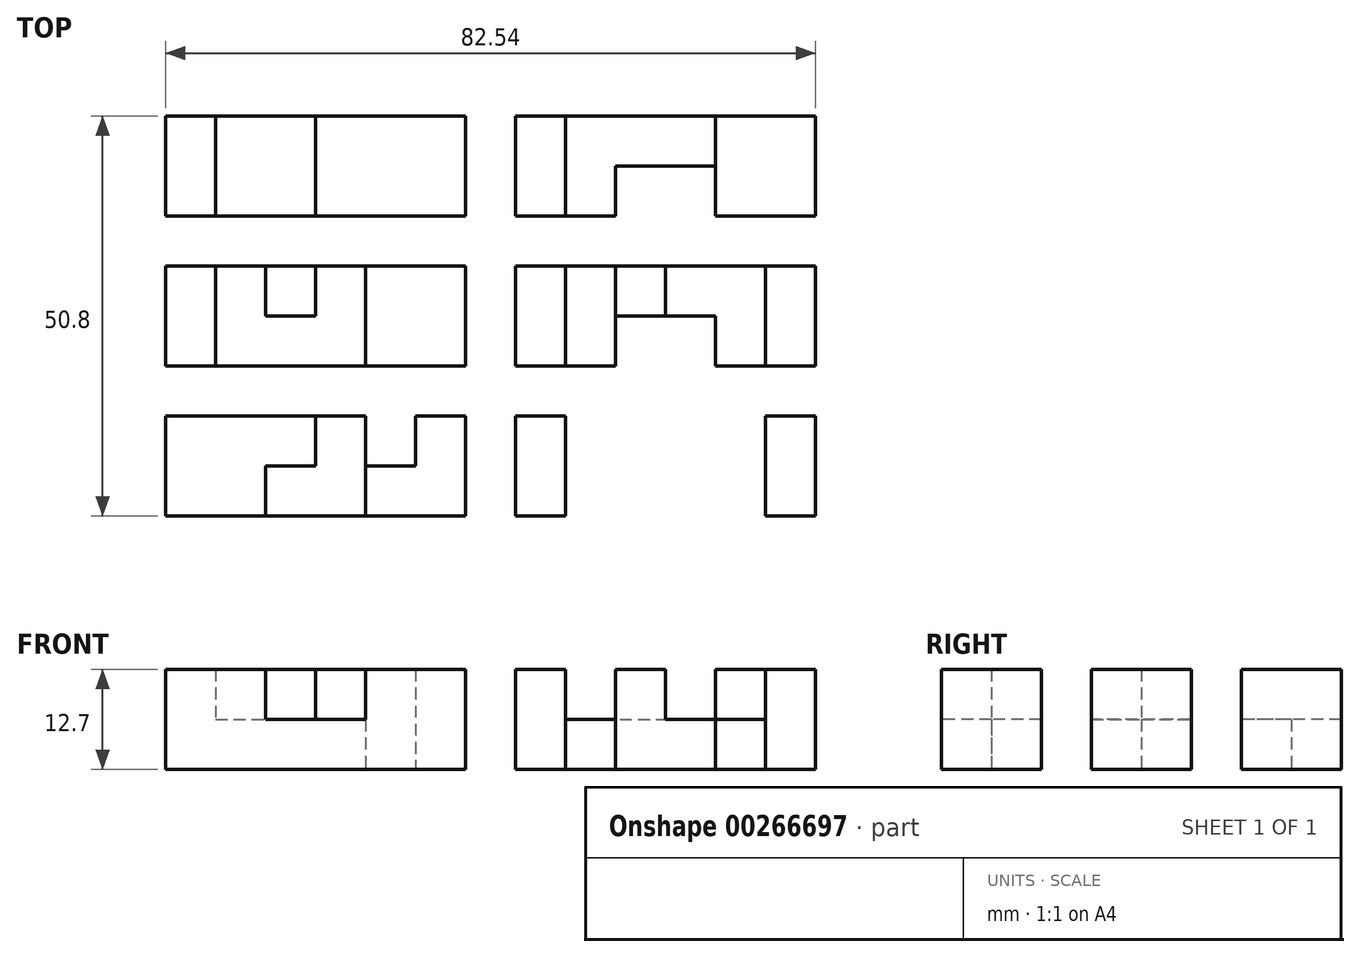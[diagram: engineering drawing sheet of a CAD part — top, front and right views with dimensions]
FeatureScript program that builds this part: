
annotation { "Feature Type Name" : "Feature", "Feature Type Description" : "" }
export const myFeature = defineFeature(function(context is Context, id is Id, definition is map)
    precondition{}
    {
        {
            var Q0;
            Q0=qCreatedBy(makeId("Top.planeOp"),FACE);
            var sketch = newSketch(context, id + "F0", { "sketchPlane" : qUnion([Q0])});
            skLineSegment(sketch, "E0.bottom", {"start": v(41.28, -25.4) * mm, "end": v(28.58, -25.4) * mm});
            skLineSegment(sketch, "E0.left", {"start": v(41.28, -25.4) * mm, "end": v(41.28, -12.7) * mm});
            skLineSegment(sketch, "E0.right", {"start": v(-41.28, -25.4) * mm, "end": v(-41.28, -12.7) * mm});
            skPoint(sketch, "E0.middle", {"position": v(0, 0) * mm});
            skLineSegment(sketch, "E1.right", {"start": v(-3.18, 25.4) * mm, "end": v(-3.18, 12.7) * mm});
            skLineSegment(sketch, "E2.top", {"start": v(41.28, 12.7) * mm, "end": v(28.58, 12.7) * mm});
            skLineSegment(sketch, "E2.left", {"start": v(41.28, 25.4) * mm, "end": v(41.28, 12.7) * mm});
            skLineSegment(sketch, "E2.right", {"start": v(3.18, 25.4) * mm, "end": v(3.18, 12.7) * mm});
            skLineSegment(sketch, "E3.bottom", {"start": v(-41.28, -25.4) * mm, "end": v(-15.88, -25.4) * mm});
            skLineSegment(sketch, "E3.top", {"start": v(-41.28, -12.7) * mm, "end": v(-15.88, -12.7) * mm});
            skLineSegment(sketch, "E3.right", {"start": v(-3.18, -25.4) * mm, "end": v(-3.18, -12.7) * mm});
            skLineSegment(sketch, "E4.top", {"start": v(41.28, -12.7) * mm, "end": v(3.18, -12.7) * mm});
            skLineSegment(sketch, "E4.right", {"start": v(3.17, -25.4) * mm, "end": v(3.17, -12.7) * mm});
            skLineSegment(sketch, "E5", {"start": v(-22.23, 25.4) * mm, "end": v(-22.23, 12.7) * mm});
            skLineSegment(sketch, "E6", {"start": v(28.57, 19.05) * mm, "end": v(15.88, 19.05) * mm});
            skLineSegment(sketch, "E7.right", {"start": v(-34.93, 12.7) * mm, "end": v(-34.93, 25.4) * mm});
            skLineSegment(sketch, "E8.right", {"start": v(-28.57, -19.05) * mm, "end": v(-28.57, -25.4) * mm});
            skLineSegment(sketch, "E9.left", {"start": v(-9.53, -12.7) * mm, "end": v(-9.53, -19.05) * mm});
            skLineSegment(sketch, "E9.right", {"start": v(-15.88, -12.7) * mm, "end": v(-15.88, -25.4) * mm});
            skLineSegment(sketch, "E10", {"start": v(-22.23, -12.7) * mm, "end": v(-22.23, -19.05) * mm});
            skLineSegment(sketch, "E11.top", {"start": v(9.52, -25.4) * mm, "end": v(15.88, -25.4) * mm});
            skLineSegment(sketch, "E11.left", {"start": v(9.52, 25.4) * mm, "end": v(9.52, 12.7) * mm});
            skLineSegment(sketch, "E11.right", {"start": v(15.88, 19.05) * mm, "end": v(15.88, 12.7) * mm});
            skLineSegment(sketch, "E12.top", {"start": v(34.93, -25.4) * mm, "end": v(28.58, -25.4) * mm});
            skLineSegment(sketch, "E12.right", {"start": v(28.57, 25.4) * mm, "end": v(28.58, 12.7) * mm});
            skLineSegment(sketch, "E13.trimOffspring", {"start": v(9.52, -19.05) * mm, "end": v(9.52, -25.4) * mm});
            skLineSegment(sketch, "E14.trimOffspring", {"start": v(15.88, -19.05) * mm, "end": v(15.88, -25.4) * mm});
            skLineSegment(sketch, "E15.trimOffspring", {"start": v(28.58, -19.05) * mm, "end": v(28.58, -25.4) * mm});
            skLineSegment(sketch, "E16.trimOffspring", {"start": v(34.93, -12.7) * mm, "end": v(34.93, -25.4) * mm});
            skLineSegment(sketch, "E17.bottom", {"start": v(-41.28, -6.35) * mm, "end": v(-3.18, -6.35) * mm});
            skLineSegment(sketch, "E17.top", {"start": v(-41.28, 6.35) * mm, "end": v(-3.18, 6.35) * mm});
            skLineSegment(sketch, "E17.left", {"start": v(-41.28, -6.35) * mm, "end": v(-41.28, 6.35) * mm});
            skLineSegment(sketch, "E18.left", {"start": v(-3.18, 6.35) * mm, "end": v(-3.18, -6.35) * mm});
            skLineSegment(sketch, "E18.right", {"start": v(3.18, 6.35) * mm, "end": v(3.18, -6.35) * mm});
            skPoint(sketch, "E19.orphan", {"position": v(41.28, 0) * mm});
            skPoint(sketch, "E20.start.orphan", {"position": v(-41.28, 0) * mm});
            skLineSegment(sketch, "E21.trimOffspring", {"start": v(41.28, 12.7) * mm, "end": v(41.28, 25.4) * mm});
            skLineSegment(sketch, "E22", {"start": v(41.28, 6.35) * mm, "end": v(41.28, -6.35) * mm});
            skLineSegment(sketch, "E23", {"start": v(-28.57, 0) * mm, "end": v(-22.23, 0) * mm});
            skLineSegment(sketch, "E24.trimOffspring", {"start": v(3.18, 6.35) * mm, "end": v(22.23, 6.35) * mm});
            skLineSegment(sketch, "E25.trimOffspring", {"start": v(3.18, -6.35) * mm, "end": v(15.88, -6.35) * mm});
            skLineSegment(sketch, "E26", {"start": v(-34.93, 6.35) * mm, "end": v(-34.93, -6.35) * mm});
            skLineSegment(sketch, "E27", {"start": v(-28.57, 0) * mm, "end": v(-28.57, 6.35) * mm});
            skLineSegment(sketch, "E28", {"start": v(-22.23, 6.35) * mm, "end": v(-22.23, 0) * mm});
            skLineSegment(sketch, "E29", {"start": v(-15.88, -6.35) * mm, "end": v(-15.88, 6.35) * mm});
            skLineSegment(sketch, "E30", {"start": v(9.52, 6.35) * mm, "end": v(9.52, -6.35) * mm});
            skLineSegment(sketch, "E31", {"start": v(15.88, -6.35) * mm, "end": v(15.88, 6.35) * mm});
            skLineSegment(sketch, "E32", {"start": v(22.23, 6.35) * mm, "end": v(22.23, 0) * mm});
            skLineSegment(sketch, "E33", {"start": v(28.58, -6.35) * mm, "end": v(28.58, 0) * mm});
            skLineSegment(sketch, "E34", {"start": v(34.92, 6.35) * mm, "end": v(34.93, -6.35) * mm});
            skLineSegment(sketch, "E35.trimOffspring", {"start": v(-41.28, 12.7) * mm, "end": v(-41.28, 25.4) * mm});
            skLineSegment(sketch, "E36", {"start": v(9.52, -19.05) * mm, "end": v(9.52, -12.7) * mm});
            skPoint(sketch, "E37.orphan", {"position": v(-41.28, 19.05) * mm});
            skPoint(sketch, "E38.start.orphan", {"position": v(-3.18, 19.05) * mm});
            skLineSegment(sketch, "E39.trimOffspring", {"start": v(15.88, -25.4) * mm, "end": v(3.17, -25.4) * mm});
            skPoint(sketch, "E40.orphan", {"position": v(22.23, -25.4) * mm});
            skPoint(sketch, "E41.end.orphan", {"position": v(22.23, -12.7) * mm});
            skPoint(sketch, "E42.trimOffspring.end.orphan", {"position": v(41.28, -19.05) * mm});
            skLineSegment(sketch, "E43.trimOffspring", {"start": v(15.88, -19.05) * mm, "end": v(28.58, -19.05) * mm});
            skLineSegment(sketch, "E44.trimOffspring", {"start": v(-9.53, -12.7) * mm, "end": v(-3.18, -12.7) * mm});
            skLineSegment(sketch, "E45.trimOffspring", {"start": v(-15.88, -19.05) * mm, "end": v(-9.53, -19.05) * mm});
            skPoint(sketch, "E46.orphan", {"position": v(-22.23, -25.4) * mm});
            skLineSegment(sketch, "E47.trimOffspring", {"start": v(-28.57, -19.05) * mm, "end": v(-22.23, -19.05) * mm});
            skPoint(sketch, "E48.start.orphan", {"position": v(-41.28, -19.05) * mm});
            skLineSegment(sketch, "E49.trimOffspring", {"start": v(15.88, 12.7) * mm, "end": v(3.18, 12.7) * mm});
            skPoint(sketch, "E50.orphan", {"position": v(22.23, 12.7) * mm});
            skPoint(sketch, "E51.orphan", {"position": v(41.28, 19.05) * mm});
            skPoint(sketch, "E52.start.orphan", {"position": v(22.23, 25.4) * mm});
            skPoint(sketch, "E53.trimOffspring.end.orphan", {"position": v(3.18, 19.05) * mm});
            skLineSegment(sketch, "E54.trimOffspring", {"start": v(28.58, -6.35) * mm, "end": v(41.28, -6.35) * mm});
            skLineSegment(sketch, "E55.trimOffspring", {"start": v(22.23, 0) * mm, "end": v(28.58, 0) * mm});
            skLineSegment(sketch, "E56", {"start": v(-41.28, 25.4) * mm, "end": v(-3.18, 25.4) * mm});
            skLineSegment(sketch, "E57", {"start": v(-3.18, 12.7) * mm, "end": v(-41.28, 12.7) * mm});
            skLineSegment(sketch, "E58.trimOffspring", {"start": v(9.52, 25.4) * mm, "end": v(3.17, 25.4) * mm});
            skLineSegment(sketch, "E59.trimOffspring", {"start": v(34.92, 6.35) * mm, "end": v(41.28, 6.35) * mm});
            skLineSegment(sketch, "E60", {"start": v(9.52, 25.4) * mm, "end": v(41.28, 25.4) * mm});
            skLineSegment(sketch, "E61", {"start": v(22.23, 6.35) * mm, "end": v(34.92, 6.35) * mm});
            skLineSegment(sketch, "E62", {"start": v(22.23, 0) * mm, "end": v(15.88, 0) * mm});
            skLineSegment(sketch, "E63.trimOffspring", {"start": v(-15.88, -25.4) * mm, "end": v(-41.28, -25.4) * mm});
            skLineSegment(sketch, "E64", {"start": v(-15.88, -25.4) * mm, "end": v(-3.18, -25.4) * mm});
            skSolve(sketch);
        }
        {
            var Q0;
            {var subQ2=sQuery(id+"F0.wireOp",EDGE,"E7.right");Q0=makeQuery(id+"F0.imprint","IMPRINT",FACE,{"disambiguationData":[TD([[makeQuery(id+"F0.imprint","IMPRINT",EDGE,{"derivedFrom":subQ2}),1.0]])]});}
            var Q1;
            {var subQ1=sQuery(id+"F0.wireOp",EDGE,"E1.right");Q1=makeQuery(id+"F0.imprint","IMPRINT",FACE,{"disambiguationData":[TD([[makeQuery(id+"F0.imprint","IMPRINT",EDGE,{"derivedFrom":subQ1}),-1.0]])]});}
            var Q2;
            {var subQ2=sQuery(id+"F0.wireOp",EDGE,"E26");Q2=makeQuery(id+"F0.imprint","IMPRINT",FACE,{"disambiguationData":[TD([[makeQuery(id+"F0.imprint","IMPRINT",EDGE,{"derivedFrom":subQ2}),-1.0]])]});}
            var Q3;
            {var subQ0=sQuery(id+"F0.wireOp",EDGE,"E18.left");Q3=makeQuery(id+"F0.imprint","IMPRINT",FACE,{"disambiguationData":[TD([[makeQuery(id+"F0.imprint","IMPRINT",EDGE,{"derivedFrom":subQ0}),-1.0]])]});}
            var Q4;
            Q4=makeQuery(id+"F0.imprint","IMPRINT",FACE,{"disambiguationData":[TD([[makeQuery(id+"F0.imprint","IMPRINT",EDGE,{"derivedFrom":sQuery(id+"F0.wireOp",EDGE,"E23")}),1.0]])]});
            var Q5;
            {var subQ1=sQuery(id+"F0.wireOp",EDGE,"E0.right");Q5=makeQuery(id+"F0.imprint","IMPRINT",FACE,{"disambiguationData":[TD([[makeQuery(id+"F0.imprint","IMPRINT",EDGE,{"derivedFrom":subQ1}),-1.0]])]});}
            var Q6;
            {var subQ1=sQuery(id+"F0.wireOp",EDGE,"E3.right");Q6=makeQuery(id+"F0.imprint","IMPRINT",FACE,{"disambiguationData":[TD([[makeQuery(id+"F0.imprint","IMPRINT",EDGE,{"derivedFrom":subQ1}),1.0]])]});}
            var Q7;
            {var subQ1=sQuery(id+"F0.wireOp",EDGE,"E2.top");Q7=makeQuery(id+"F0.imprint","IMPRINT",FACE,{"disambiguationData":[TD([[makeQuery(id+"F0.imprint","IMPRINT",EDGE,{"derivedFrom":subQ1}),-1.0]])]});}
            var Q8;
            {var subQ0=sQuery(id+"F0.wireOp",EDGE,"E2.right");Q8=makeQuery(id+"F0.imprint","IMPRINT",FACE,{"disambiguationData":[TD([[makeQuery(id+"F0.imprint","IMPRINT",EDGE,{"derivedFrom":subQ0}),1.0]])]});}
            var Q9;
            {var subQ0=sQuery(id+"F0.wireOp",EDGE,"E18.right");Q9=makeQuery(id+"F0.imprint","IMPRINT",FACE,{"disambiguationData":[TD([[makeQuery(id+"F0.imprint","IMPRINT",EDGE,{"derivedFrom":subQ0}),1.0]])]});}
            var Q10;
            {var subQ3=sQuery(id+"F0.wireOp",EDGE,"E32");Q10=makeQuery(id+"F0.imprint","IMPRINT",FACE,{"disambiguationData":[TD([[makeQuery(id+"F0.imprint","IMPRINT",EDGE,{"derivedFrom":subQ3}),-1.0]])]});}
            var Q11;
            {var subQ0=sQuery(id+"F0.wireOp",EDGE,"E22");Q11=makeQuery(id+"F0.imprint","IMPRINT",FACE,{"disambiguationData":[TD([[makeQuery(id+"F0.imprint","IMPRINT",EDGE,{"derivedFrom":subQ0}),-1.0]])]});}
            var Q12;
            Q12=makeQuery(id+"F0.imprint","IMPRINT",FACE,{"disambiguationData":[TD([[makeQuery(id+"F0.imprint","IMPRINT",EDGE,{"derivedFrom":sQuery(id+"F0.wireOp",EDGE,"E0.bottom")}),-1.0]])]});
            var Q13;
            {var subQ1=sQuery(id+"F0.wireOp",EDGE,"E4.right");Q13=makeQuery(id+"F0.imprint","IMPRINT",FACE,{"disambiguationData":[TD([[makeQuery(id+"F0.imprint","IMPRINT",EDGE,{"derivedFrom":subQ1}),-1.0]])]});}
            extrude(context, id + "F1", {"entities" : qUnion([Q0, Q1, Q2, Q3, Q4, Q5, Q6, Q7, Q8, Q9, Q10, Q11, Q12, Q13]), "depth" : 12.7 * mm});
        }
        {
            var Q0;
            Q0=makeQuery(id+"F0.imprint","IMPRINT",FACE,{"disambiguationData":[TD([[makeQuery(id+"F0.imprint","IMPRINT",EDGE,{"derivedFrom":sQuery(id+"F0.wireOp",EDGE,"E12.top")}),-1.0]])]});
            var Q1;
            {var subQ6=sQuery(id+"F0.wireOp",EDGE,"E8.right");Q1=makeQuery(id+"F0.imprint","IMPRINT",FACE,{"disambiguationData":[TD([[makeQuery(id+"F0.imprint","IMPRINT",EDGE,{"derivedFrom":subQ6}),1.0]])]});}
            var Q2;
            {var subQ4=sQuery(id+"F0.wireOp",EDGE,"E30");Q2=makeQuery(id+"F0.imprint","IMPRINT",FACE,{"disambiguationData":[TD([[makeQuery(id+"F0.imprint","IMPRINT",EDGE,{"derivedFrom":subQ4}),1.0]])]});}
            var Q3;
            {var subQ2=sQuery(id+"F0.wireOp",EDGE,"E5");Q3=makeQuery(id+"F0.imprint","IMPRINT",FACE,{"disambiguationData":[TD([[makeQuery(id+"F0.imprint","IMPRINT",EDGE,{"derivedFrom":subQ2}),-1.0]])]});}
            var Q4;
            {var subQ3=sQuery(id+"F0.wireOp",EDGE,"E32");Q4=makeQuery(id+"F0.imprint","IMPRINT",FACE,{"disambiguationData":[TD([[makeQuery(id+"F0.imprint","IMPRINT",EDGE,{"derivedFrom":subQ3}),1.0]])]});}
            var Q5;
            {var subQ5=sQuery(id+"F0.wireOp",EDGE,"E6");Q5=makeQuery(id+"F0.imprint","IMPRINT",FACE,{"disambiguationData":[TD([[makeQuery(id+"F0.imprint","IMPRINT",EDGE,{"derivedFrom":subQ5}),-1.0]])]});}
            var Q6;
            Q6=makeQuery(id+"F0.imprint","IMPRINT",FACE,{"disambiguationData":[TD([[makeQuery(id+"F0.imprint","IMPRINT",EDGE,{"derivedFrom":sQuery(id+"F0.wireOp",EDGE,"E23")}),-1.0]])]});
            extrude(context, id + "F2", {"entities" : qUnion([Q0, Q1, Q2, Q3, Q4, Q5, Q6]), "operationType" : NewBodyOperationType.ADD, "depth" : 6.35 * mm});
        }
    });
